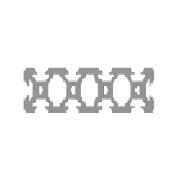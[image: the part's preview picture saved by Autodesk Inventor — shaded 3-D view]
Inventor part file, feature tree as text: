
AUTODESK INVENTOR PART (.ipt)
format: ipt  version: 2013 (Build 170138000, 138)  size: 285,184 bytes
history: native  units: mm
features: other x4, plane x3, split x2, sketch x2
ambient origin geometry x8: Origin, YZ Plane, XZ Plane, XY Plane, X Axis, Y Axis, Z Axis, Center Point
bodies: Solid1 (feature_tree), Body (feature_tree)
feature tree (11):
  other  "Driven Length"
  other  "Frame Generator"
  other  "Start Plane"
  other  "End Plane"
  plane  "Work Plane8"
  split  "Split1"
  plane  "Work Plane9"
  split  "Split2"
  sketch  "Sketch10"  dims[d0=10.0mm]
  plane  "Work Plane7"
  sketch  "Sketch11"  dims[d1=10.0mm d2=10.0mm d3=4.2mm d4=1.5mm d5=45.0deg d6=1.64mm d7=1.8mm d8=10.0mm d9=2.84mm d11=135.0deg d12=1.96mm d13=5.68mm d14=2.0mm d17=10.0mm d18=465.0mm d19=0.13mm d20=0.0mm d29=90.0deg d22=455.0mm]
